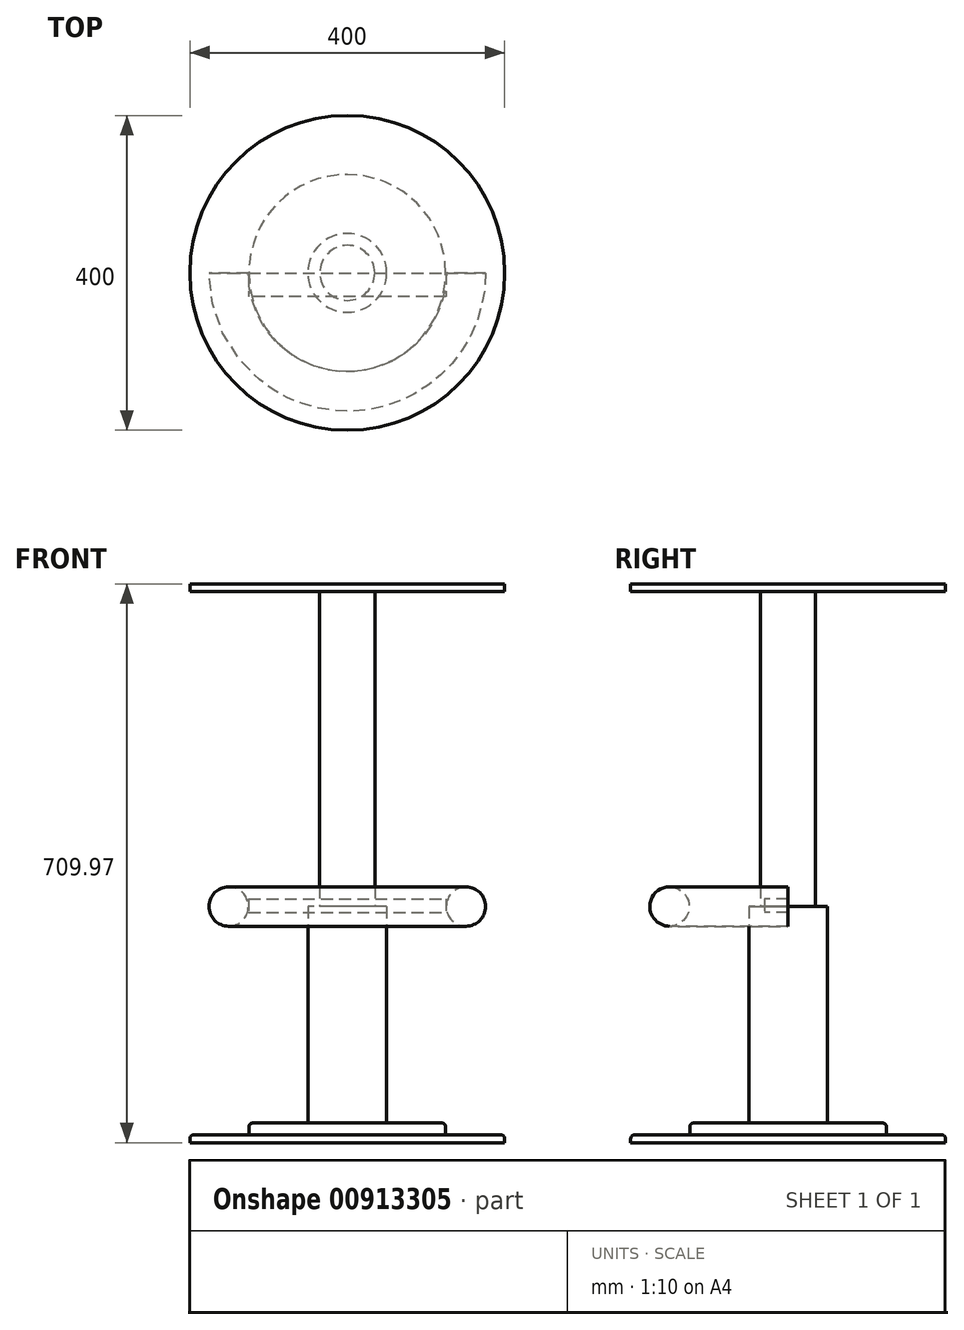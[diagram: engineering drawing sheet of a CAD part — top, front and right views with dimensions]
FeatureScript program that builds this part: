
annotation { "Feature Type Name" : "Feature", "Feature Type Description" : "" }
export const myFeature = defineFeature(function(context is Context, id is Id, definition is map)
    precondition{}
    {
        {
            var Q0;
            Q0=qCreatedBy(makeId("Top.planeOp"),FACE);
            cPlane(context, id + "F0", {"entities" : qUnion([Q0]), "cplaneType" : CPlaneType.OFFSET, "offset" : 299.97 * mm, "oppositeDirection" : true, "width" : 152.4 * mm, "height" : 152.4 * mm});
        }
        {
            var Q0;
            Q0=qCreatedBy(id+"F0.planeOp",FACE);
            var sketch = newSketch(context, id + "F1", { "sketchPlane" : qUnion([Q0])});
            skCircle(sketch, "E0", {"center": v(0, 0) * mm, "radius": 200 * mm});
            skSolve(sketch);
        }
        {
            var Q0;
            Q0=qSketchRegion(id+"F1",true);
            extrude(context, id + "F2", {"entities" : qUnion([Q0]), "depth" : 10 * mm, "offsetDistance" : 25.4 * mm});
        }
        {
            var Q0;
            Q0=makeQuery(id+"F2.opExtrude","CAP_FACE",FACE,{"disambiguationData":[OSD([sQuery(id+"F1.wireOp",EDGE,"E0")])],"isStart":false});
            var sketch = newSketch(context, id + "F3", { "sketchPlane" : qUnion([Q0])});
            skCircle(sketch, "E1", {"center": v(0, 0) * mm, "radius": 125 * mm});
            skSolve(sketch);
        }
        {
            var Q0;
            Q0=qSketchRegion(id+"F3",true);
            extrude(context, id + "F4", {"entities" : qUnion([Q0]), "operationType" : NewBodyOperationType.ADD, "depth" : 15 * mm, "offsetDistance" : 25.4 * mm});
        }
        {
            var Q0;
            Q0=makeQuery(id+"F2.opExtrude","CAP_EDGE",EDGE,{"disambiguationData":[OSD([sQuery(id+"F1.wireOp",EDGE,"E0")])],"isStart":false});
            var Q1;
            Q1=makeQuery(id+"F4.opExtrude","CAP_EDGE",EDGE,{"disambiguationData":[OSD([sQuery(id+"F3.wireOp",EDGE,"E1")])],"isStart":false});
            fillet(context, id + "F5", {"entities" : qUnion([Q0, Q1]), "radius" : 5.08 * mm, "tangentPropagation" : true, "allowEdgeOverflow" : false});
        }
        {
            var Q0;
            Q0=makeQuery(id+"F4.opExtrude","CAP_FACE",FACE,{"disambiguationData":[OSD([sQuery(id+"F3.wireOp",EDGE,"E1")])],"isStart":false});
            var sketch = newSketch(context, id + "F6", { "sketchPlane" : qUnion([Q0])});
            skCircle(sketch, "E2", {"center": v(0, 0) * mm, "radius": 50 * mm});
            skSolve(sketch);
        }
        {
            var Q0;
            Q0=qSketchRegion(id+"F6",true);
            extrude(context, id + "F7", {"entities" : qUnion([Q0]), "operationType" : NewBodyOperationType.ADD, "depth" : 275 * mm, "offsetDistance" : 25.4 * mm});
        }
        {
            var Q0;
            Q0=qCreatedBy(makeId("Top.planeOp"),FACE);
            var sketch = newSketch(context, id + "F8", { "sketchPlane" : qUnion([Q0])});
            skLineSegment(sketch, "E3", {"start": v(-49.8, 0) * mm, "end": v(-125.3, 0) * mm});
            skLineSegment(sketch, "E4", {"start": v(50, 0) * mm, "end": v(125.26, 0) * mm});
            skLineSegment(sketch, "E5", {"start": v(-125.3, 0) * mm, "end": v(-175.3, 0) * mm});
            skLineSegment(sketch, "E6", {"start": v(125.26, 0) * mm, "end": v(175.26, 0) * mm});
            skLineSegment(sketch, "E7", {"start": v(-125.3, 0) * mm, "end": v(-125.3, -30) * mm});
            skLineSegment(sketch, "E8", {"start": v(-125.3, 0) * mm, "end": v(125.26, 0) * mm});
            skLineSegment(sketch, "E9", {"start": v(125.26, 0) * mm, "end": v(125.26, -30) * mm});
            skLineSegment(sketch, "E10", {"start": v(125.26, -30) * mm, "end": v(-125.3, -30) * mm});
            skSolve(sketch);
        }
        {
            var Q0;
            Q0=qCreatedBy(makeId("Front.planeOp"),FACE);
            var sketch = newSketch(context, id + "F9", { "sketchPlane" : qUnion([Q0])});
            skCircle(sketch, "E11", {"center": v(-150.71, 0) * mm, "radius": 25 * mm});
            skSolve(sketch);
        }
        {
            var Q0;
            Q0=qSketchRegion(id+"F9",true);
            var Q1;
            Q1=makeQuery(id+"F7.opExtrude","SWEPT_FACE",FACE,{"disambiguationData":[OSD([sQuery(id+"F6.wireOp",EDGE,"E2")])]});
            revolve(context, id + "F10", {"surfaceOperationType" : NewSurfaceOperationType.NEW, "entities" : qUnion([Q0]), "axis" : qUnion([Q1]), "revolveType" : RevolveType.ONE_DIRECTION, "oppositeDirection" : true, "angle" : 180 * degree});
        }
        {
            var Q0;
            {var subQ0=sQuery(id+"F8.wireOp",EDGE,"E7");Q0=makeQuery(id+"F8.imprint","IMPRINT",FACE,{"disambiguationData":[TD([[makeQuery(id+"F8.imprint","IMPRINT",EDGE,{"derivedFrom":subQ0}),1.0]])]});}
            extrude(context, id + "F11", {"entities" : qUnion([Q0]), "depth" : 17 * mm, "offsetDistance" : 25.4 * mm});
        }
        {
            var Q0;
            Q0=makeQuery(id+"F11.opExtrude","SWEPT_BODY",BODY,{"disambiguationData":[OSD([sQuery(id+"F8.wireOp",EDGE,"E7")])]});
            transform(context, id + "F12", {"entities" : qUnion([Q0]), "transformType" : TransformType.TRANSLATION_3D, "dx" : 0 * mm, "dy" : 0 * mm, "dz" : -7.5 * mm, "makeCopy" : false});
        }
        {
            var Q0;
            Q0=qCreatedBy(makeId("Top.planeOp"),FACE);
            var sketch = newSketch(context, id + "F13", { "sketchPlane" : qUnion([Q0])});
            skCircle(sketch, "E12", {"center": v(0, 0) * mm, "radius": 35 * mm});
            skSolve(sketch);
        }
        {
            var Q0;
            Q0=qSketchRegion(id+"F13",true);
            extrude(context, id + "F14", {"entities" : qUnion([Q0]), "depth" : 400 * mm, "offsetDistance" : 25.4 * mm});
        }
        {
            var Q0;
            Q0=makeQuery(id+"F14.opExtrude","CAP_FACE",FACE,{"disambiguationData":[OSD([sQuery(id+"F13.wireOp",EDGE,"E12")])],"isStart":false});
            var sketch = newSketch(context, id + "F15", { "sketchPlane" : qUnion([Q0])});
            skCircle(sketch, "E13", {"center": v(0, 0) * mm, "radius": 200 * mm});
            skSolve(sketch);
        }
        {
            var Q0;
            Q0=qSketchRegion(id+"F15",true);
            extrude(context, id + "F16", {"entities" : qUnion([Q0]), "operationType" : NewBodyOperationType.ADD, "depth" : 10 * mm, "offsetDistance" : 25.4 * mm});
        }
    });
